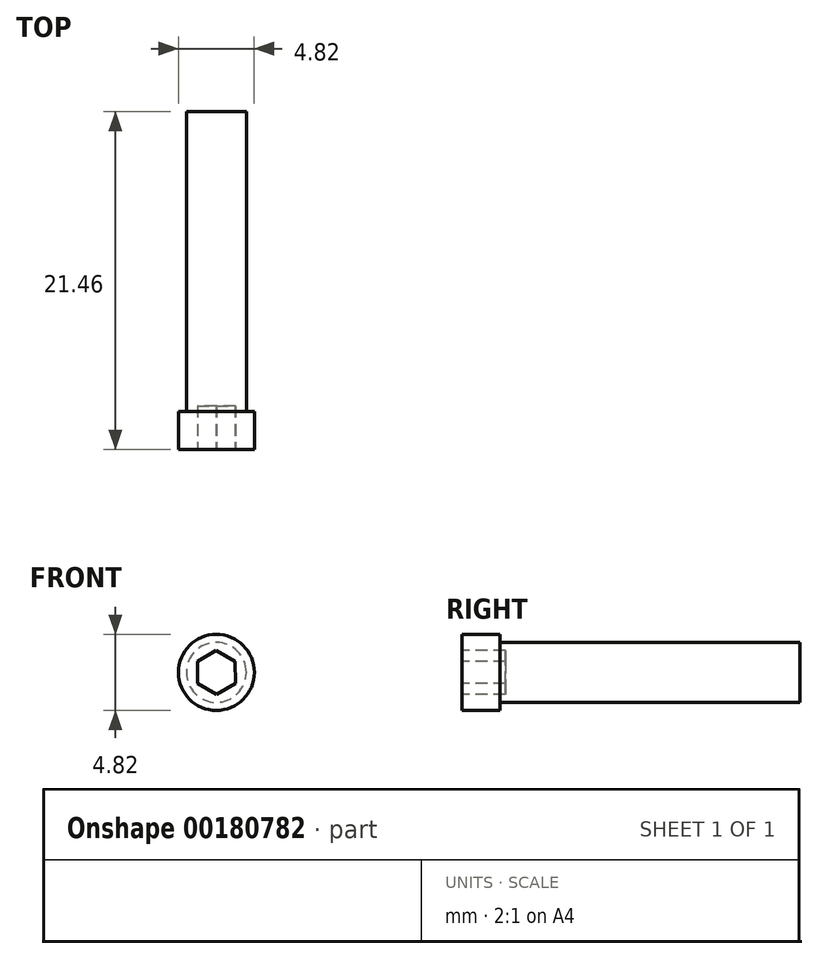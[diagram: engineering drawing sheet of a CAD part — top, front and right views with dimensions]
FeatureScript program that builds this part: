
annotation { "Feature Type Name" : "Feature", "Feature Type Description" : "" }
export const myFeature = defineFeature(function(context is Context, id is Id, definition is map)
    precondition{}
    {
        {
            var Q0;
            Q0=qCreatedBy(makeId("Front.planeOp"),FACE);
            var sketch = newSketch(context, id + "F0", { "sketchPlane" : qUnion([Q0])});
            skCircle(sketch, "E0", {"center": v(0, 0) * mm, "radius": 1.9 * mm});
            skSolve(sketch);
        }
        {
            var Q0;
            Q0 = qSketchRegion(id + "F0", true);
            extrude(context, id + "F1", {"entities" : qUnion([Q0]), "depth" : 19.05 * mm});
        }
        {
            var Q0;
            Q0=makeQuery(id+"F1.opExtrude","CAP_FACE",FACE,{"disambiguationData":[OSD([sQuery(id+"F0.wireOp",EDGE,"E0")])],"isStart":false});
            var sketch = newSketch(context, id + "F2", { "sketchPlane" : qUnion([Q0])});
            skCircle(sketch, "E1", {"center": v(0, 0) * mm, "radius": 2.41 * mm});
            skSolve(sketch);
        }
        {
            var Q0;
            Q0 = qSketchRegion(id + "F2", true);
            extrude(context, id + "F3", {"entities" : qUnion([Q0]), "operationType" : NewBodyOperationType.ADD, "depth" : 2.41 * mm});
        }
        {
            var Q0;
            Q0=makeQuery(id+"F3.opExtrude","CAP_FACE",FACE,{"disambiguationData":[OSD([sQuery(id+"F2.wireOp",EDGE,"E1")])],"isStart":false});
            var sketch = newSketch(context, id + "F4", { "sketchPlane" : qUnion([Q0])});
            skCircle(sketch, "E2.cCircle", {"center": v(0, 0) * mm, "radius": 1.2 * mm, "construction": true});
            skLineSegment(sketch, "E2.0", {"start": v(-1.2, 0.7) * mm, "end": v(0, 1.39) * mm});
            skLineSegment(sketch, "E2.1", {"start": v(0, 1.39) * mm, "end": v(1.2, 0.7) * mm});
            skLineSegment(sketch, "E2.2", {"start": v(1.2, 0.7) * mm, "end": v(1.2, -0.7) * mm});
            skLineSegment(sketch, "E2.3", {"start": v(1.2, -0.7) * mm, "end": v(0, -1.39) * mm});
            skLineSegment(sketch, "E2.4", {"start": v(0, -1.39) * mm, "end": v(-1.2, -0.7) * mm});
            skLineSegment(sketch, "E2.5", {"start": v(-1.2, -0.7) * mm, "end": v(-1.2, 0.7) * mm});
            skPoint(sketch, "E2.0.midPoint", {"position": v(-0.6, 1.04) * mm});
            skSolve(sketch);
        }
        {
            var Q0;
            Q0 = qSketchRegion(id + "F4", true);
            extrude(context, id + "F5", {"entities" : qUnion([Q0]), "operationType" : NewBodyOperationType.REMOVE, "oppositeDirection" : true, "depth" : 2.77 * mm});
        }
    });
